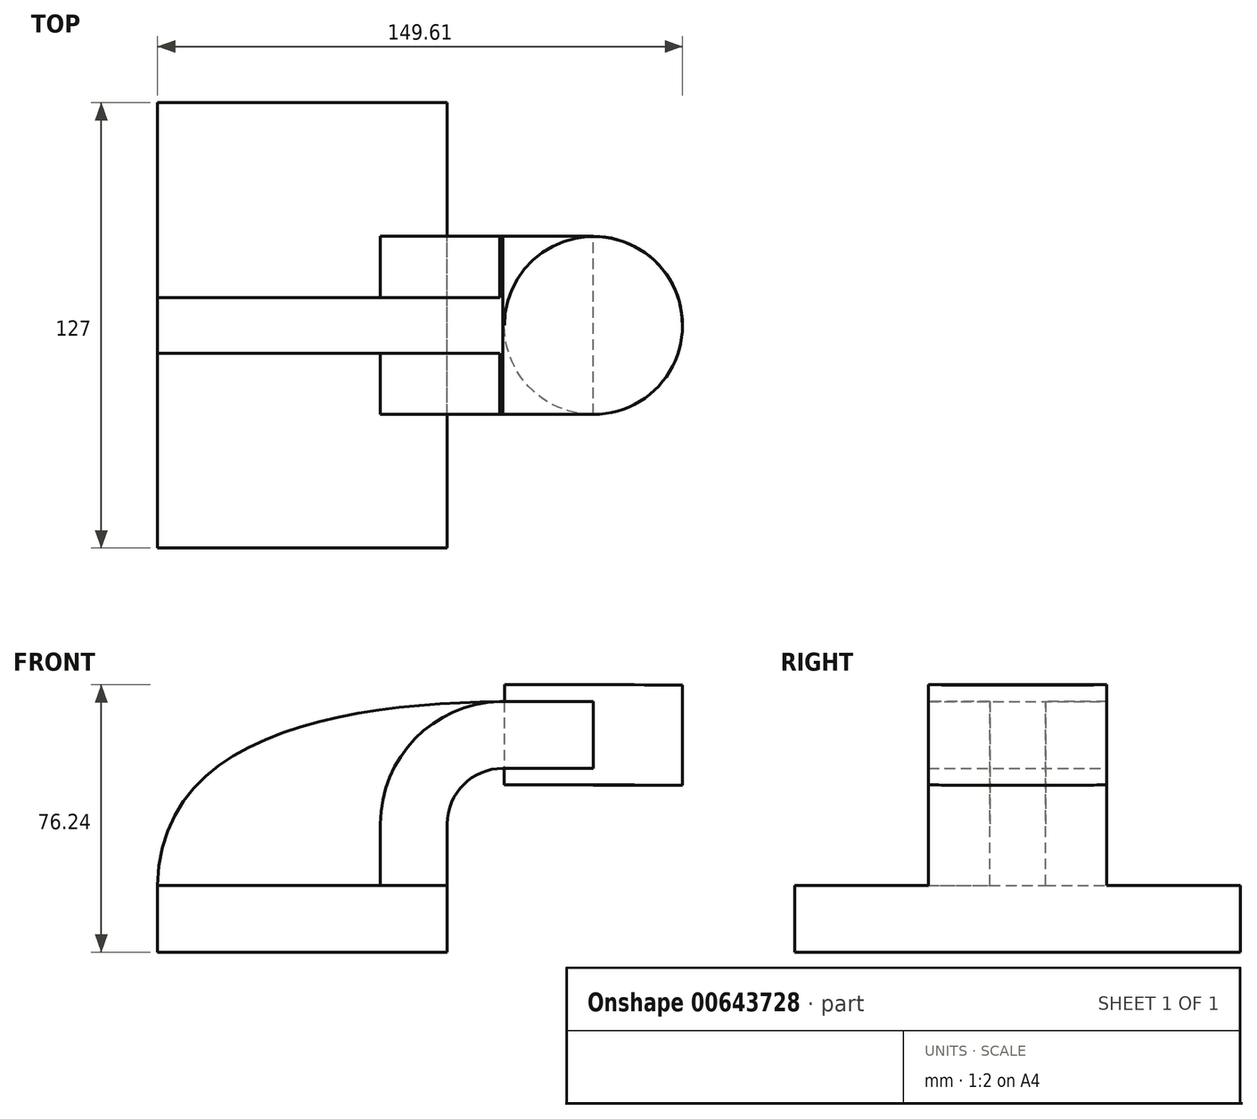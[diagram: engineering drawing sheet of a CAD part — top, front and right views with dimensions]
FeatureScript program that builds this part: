
annotation { "Feature Type Name" : "Feature", "Feature Type Description" : "" }
export const myFeature = defineFeature(function(context is Context, id is Id, definition is map)
    precondition{}
    {
        {
            var Q0;
            Q0=qCreatedBy(makeId("Front.planeOp"),FACE);
            var sketch = newSketch(context, id + "F0", { "sketchPlane" : qUnion([Q0])});
            skPoint(sketch, "E0.middle", {"position": v(0, 0) * mm});
            skLineSegment(sketch, "E1.bottom", {"start": v(41.27, 9.53) * mm, "end": v(-41.28, 9.53) * mm});
            skLineSegment(sketch, "E1.top", {"start": v(41.28, -9.52) * mm, "end": v(-41.28, -9.53) * mm});
            skLineSegment(sketch, "E1.left", {"start": v(41.28, 9.53) * mm, "end": v(41.28, -9.52) * mm});
            skLineSegment(sketch, "E1.right", {"start": v(-41.28, 9.53) * mm, "end": v(-41.27, -9.53) * mm});
            skLineSegment(sketch, "E2.bottom", {"start": v(57.53, 38.1) * mm, "end": v(108.33, 38.1) * mm});
            skLineSegment(sketch, "E2.top", {"start": v(57.53, 66.68) * mm, "end": v(108.33, 66.68) * mm});
            skLineSegment(sketch, "E2.left", {"start": v(57.53, 38.1) * mm, "end": v(57.53, 66.68) * mm});
            skLineSegment(sketch, "E2.right", {"start": v(108.33, 38.1) * mm, "end": v(108.33, 66.68) * mm});
            skPoint(sketch, "E2.middle", {"position": v(82.93, 52.39) * mm});
            skLineSegment(sketch, "E3", {"start": v(41.27, 9.53) * mm, "end": v(41.27, 27) * mm});
            skArc(sketch, "E4", {"start": v(41.28, 27) * mm, "mid": v(45.92, 38.23) * mm, "end": v(57.15, 42.88) * mm});
            skLineSegment(sketch, "E5", {"start": v(57.15, 42.88) * mm, "end": v(82.95, 42.88) * mm});
            skLineSegment(sketch, "E6.0", {"start": v(22.22, 9.53) * mm, "end": v(22.22, 27) * mm});
            skArc(sketch, "E7.0", {"start": v(22.23, 27) * mm, "mid": v(32.45, 51.7) * mm, "end": v(57.15, 61.93) * mm});
            skLineSegment(sketch, "E8.0", {"start": v(57.15, 61.93) * mm, "end": v(82.95, 61.93) * mm});
            skFitSpline(sketch, "E9", {"points": [v(-41.28, 9.53) * mm, v(57.15, 61.93) * mm], "startDerivative": vector(1.78, 133.71) * mm, "endDerivative": vector(127.27, 1.62) * mm});
            skPoint(sketch, "E10.startSnap0", {"position": v(82.93, 38.1) * mm});
            skLineSegment(sketch, "E11", {"start": v(82.93, 38.1) * mm, "end": v(82.95, 66.68) * mm});
            skSolve(sketch);
        }
        {
            var Q0;
            Q0=makeQuery(id+"F0.imprint","IMPRINT",FACE,{"disambiguationData":[TD([[makeQuery(id+"F0.imprint","IMPRINT",EDGE,{"derivedFrom":sQuery(id+"F0.wireOp",EDGE,"E1.top")}),-1.0]])]});
            extrude(context, id + "F1", {"entities" : qUnion([Q0]), "endBound" : BoundingType.SYMMETRIC, "depth" : 127 * mm, "offsetDistance" : 25.4 * mm});
        }
        {
            var Q0;
            {var subQ6=sQuery(id+"F0.wireOp",EDGE,"E3");Q0=makeQuery(id+"F0.imprint","IMPRINT",FACE,{"disambiguationData":[TD([[makeQuery(id+"F0.imprint","IMPRINT",EDGE,{"derivedFrom":subQ6}),1.0]])]});}
            var Q1;
            {var subQ0=sQuery(id+"F0.wireOp",EDGE,"E5");var subQ1=sQuery(id+"F0.wireOp",EDGE,"E2.left");var subQ2=makeQuery(id+"F0.imprint","INTERSECT",VERTEX,{"derivedFrom":[subQ1,subQ0]});Q1=makeQuery(id+"F0.imprint","IMPRINT",FACE,{"disambiguationData":[TD([[makeQuery(id+"F0.imprint","IMPRINT",EDGE,{"disambiguationData":[TD([[subQ2,-1.0]])],"derivedFrom":subQ1}),-1.0]])]});}
            extrude(context, id + "F2", {"entities" : qUnion([Q0, Q1]), "operationType" : NewBodyOperationType.ADD, "endBound" : BoundingType.SYMMETRIC, "depth" : 50.8 * mm, "offsetDistance" : 25.4 * mm});
        }
        {
            var Q0;
            {var subQ3=sQuery(id+"F0.wireOp",EDGE,"E6.0");Q0=makeQuery(id+"F0.imprint","IMPRINT",FACE,{"disambiguationData":[TD([[makeQuery(id+"F0.imprint","IMPRINT",EDGE,{"derivedFrom":subQ3}),1.0]])]});}
            extrude(context, id + "F3", {"entities" : qUnion([Q0]), "operationType" : NewBodyOperationType.ADD, "endBound" : BoundingType.SYMMETRIC, "depth" : 15.88 * mm, "offsetDistance" : 25.4 * mm});
        }
        {
            var Q0;
            {var subQ4=sQuery(id+"F0.wireOp",EDGE,"E2.right");Q0=makeQuery(id+"F0.imprint","IMPRINT",FACE,{"disambiguationData":[TD([[makeQuery(id+"F0.imprint","IMPRINT",EDGE,{"derivedFrom":subQ4}),1.0]])]});}
            var Q1;
            Q1=sQuery(id+"F0.wireOp",EDGE,"E11");
            revolve(context, id + "F4", {"entities" : qUnion([Q0]), "axis" : qUnion([Q1]), "revolveType" : RevolveType.FULL});
        }
    });
